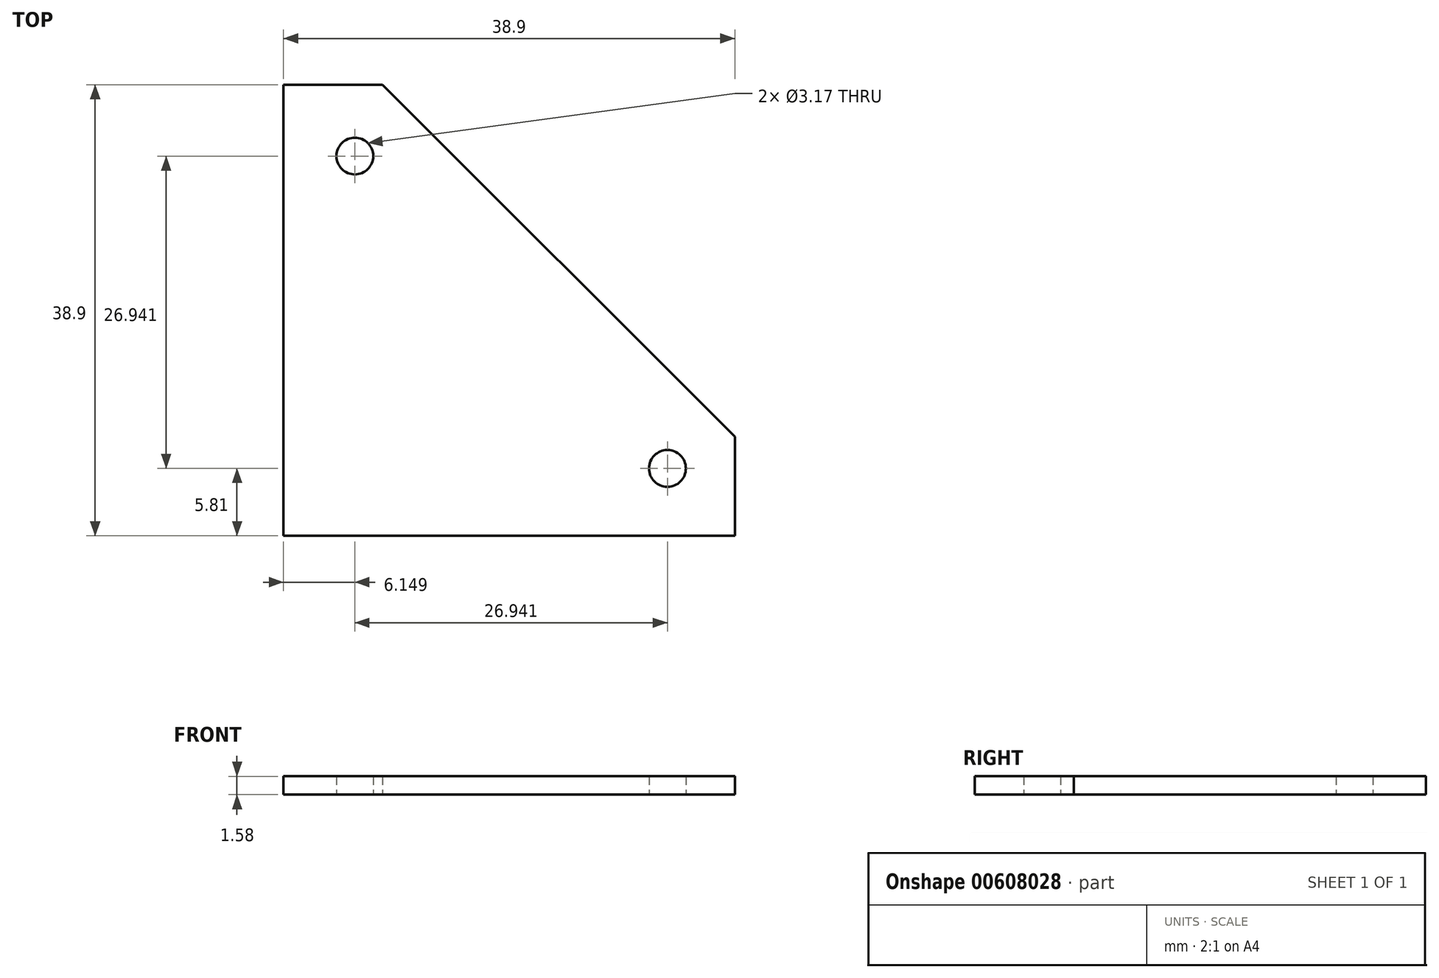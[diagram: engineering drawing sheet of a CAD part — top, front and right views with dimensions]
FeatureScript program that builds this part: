
annotation { "Feature Type Name" : "Feature", "Feature Type Description" : "" }
export const myFeature = defineFeature(function(context is Context, id is Id, definition is map)
    precondition{}
    {
        {
            var Q0;
            Q0=qCreatedBy(makeId("Top.planeOp"),FACE);
            var sketch = newSketch(context, id + "F0", { "sketchPlane" : qUnion([Q0])});
            skLineSegment(sketch, "E0", {"start": v(0, 0) * mm, "end": v(89.8, -89.8) * mm, "construction": true});
            skLineSegment(sketch, "E1", {"start": v(89.8, -89.8) * mm, "end": v(0, 0) * mm, "construction": true});
            skLineSegment(sketch, "E2", {"start": v(-26.94, 26.94) * mm, "end": v(0, 0) * mm, "construction": true});
            skCircle(sketch, "E3", {"center": v(0, 0) * mm, "radius": 1.59 * mm});
            skCircle(sketch, "E4", {"center": v(-26.94, 26.94) * mm, "radius": 1.59 * mm});
            skLineSegment(sketch, "E5", {"start": v(-33.1, -5.81) * mm, "end": v(5.81, -5.81) * mm});
            skLineSegment(sketch, "E6", {"start": v(5.81, -5.81) * mm, "end": v(5.81, 2.73) * mm});
            skLineSegment(sketch, "E7", {"start": v(5.81, 2.73) * mm, "end": v(-24.55, 33.1) * mm});
            skLineSegment(sketch, "E8", {"start": v(-24.55, 33.1) * mm, "end": v(-33.1, 33.1) * mm});
            skLineSegment(sketch, "E9", {"start": v(-33.1, 33.1) * mm, "end": v(-33.1, -5.81) * mm});
            skSolve(sketch);
        }
        {
            var Q0;
            Q0=makeQuery(id+"F0.imprint","IMPRINT",FACE,{"disambiguationData":[TD([[makeQuery(id+"F0.imprint","IMPRINT",EDGE,{"derivedFrom":sQuery(id+"F0.wireOp",EDGE,"E3")}),-1.0]])]});
            extrude(context, id + "F1", {"entities" : qUnion([Q0]), "endBound" : BoundingType.SYMMETRIC, "depth" : 1.59 * mm, "offsetDistance" : 25.4 * mm});
        }
    });
